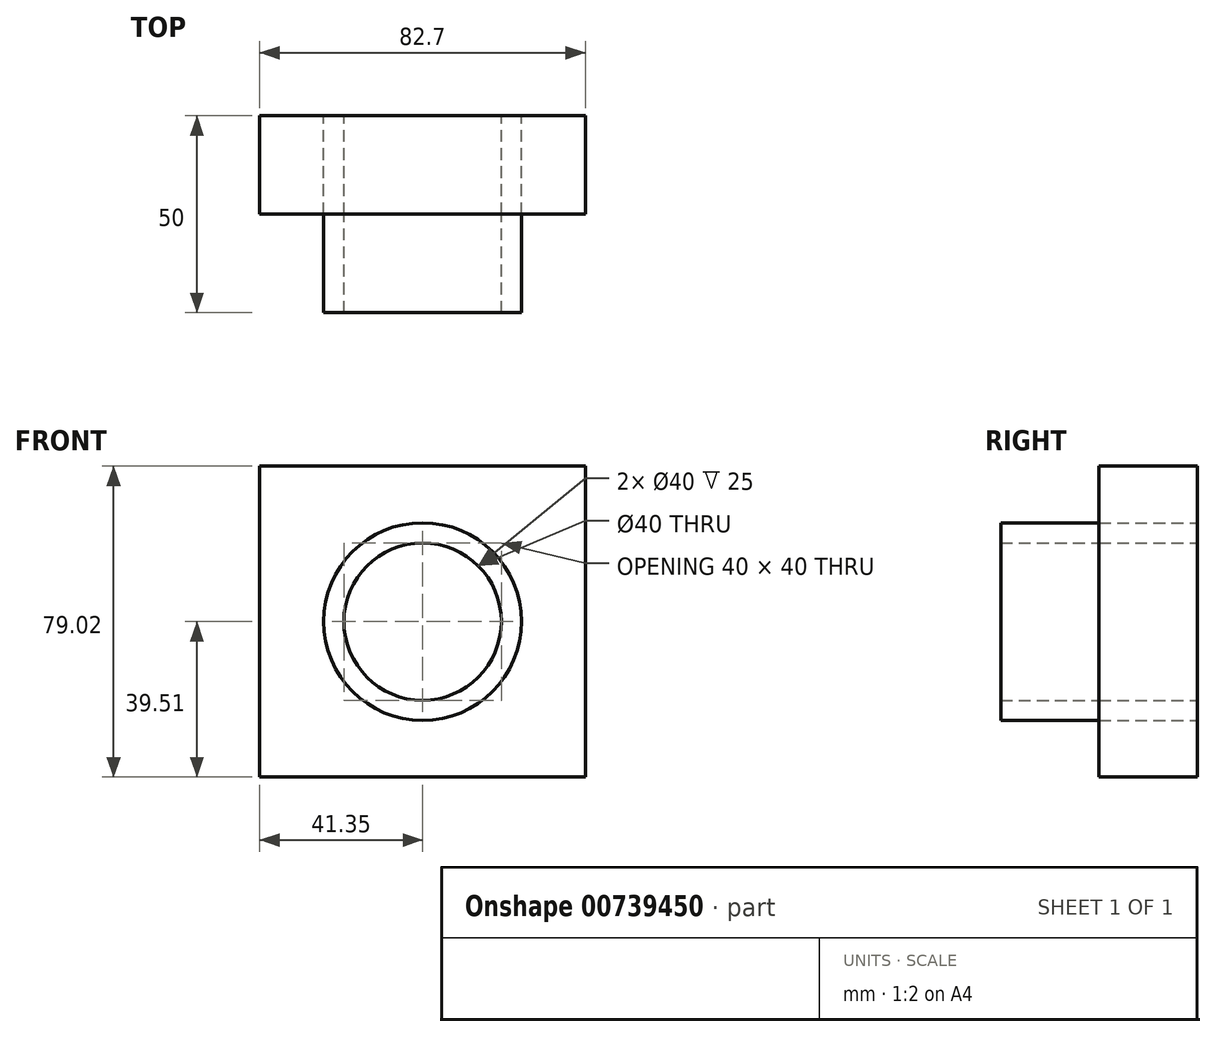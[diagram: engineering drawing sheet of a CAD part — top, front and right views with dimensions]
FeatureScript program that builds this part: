
annotation { "Feature Type Name" : "Feature", "Feature Type Description" : "" }
export const myFeature = defineFeature(function(context is Context, id is Id, definition is map)
    precondition{}
    {
        {
            var Q0;
            Q0=qCreatedBy(makeId("Front.planeOp"),FACE);
            var sketch = newSketch(context, id + "F0", { "sketchPlane" : qUnion([Q0])});
            skLineSegment(sketch, "E0.bottom", {"start": v(41.35, 39.51) * mm, "end": v(-41.35, 39.51) * mm});
            skLineSegment(sketch, "E0.top", {"start": v(41.35, -39.51) * mm, "end": v(-41.35, -39.51) * mm});
            skLineSegment(sketch, "E0.left", {"start": v(41.35, 39.51) * mm, "end": v(41.35, -39.51) * mm});
            skLineSegment(sketch, "E0.right", {"start": v(-41.35, 39.51) * mm, "end": v(-41.35, -39.51) * mm});
            skPoint(sketch, "E0.middle", {"position": v(0, 0) * mm});
            skSolve(sketch);
        }
        {
            var Q0;
            Q0=qCreatedBy(makeId("Front.planeOp"),FACE);
            var sketch = newSketch(context, id + "F1", { "sketchPlane" : qUnion([Q0])});
            skCircle(sketch, "E1", {"center": v(0, 0) * mm, "radius": 25.11 * mm});
            skSolve(sketch);
        }
        {
            var Q0;
            Q0=makeQuery(id+"F0.imprint","IMPRINT",FACE,{"disambiguationData":[TD([[makeQuery(id+"F0.imprint","IMPRINT",EDGE,{"derivedFrom":sQuery(id+"F0.wireOp",EDGE,"E0.bottom")}),1.0]])]});
            var Q1;
            Q1=makeQuery(id+"F1.imprint","IMPRINT",FACE,{"disambiguationData":[TD([[makeQuery(id+"F1.imprint","IMPRINT",EDGE,{"derivedFrom":sQuery(id+"F1.wireOp",EDGE,"E1")}),1.0]])]});
            extrude(context, id + "F2", {"entities" : qUnion([Q0, Q1]), "depth" : 25 * mm, "offsetDistance" : 25 * mm});
        }
        {
            var Q0;
            Q0=makeQuery(id+"F2.opExtrude","CAP_FACE",FACE,{"disambiguationData":[OSD([sQuery(id+"F1.wireOp",EDGE,"E1")])],"isStart":false});
            extrude(context, id + "F3", {"entities" : qUnion([Q0]), "depth" : 25 * mm, "offsetDistance" : 25 * mm});
        }
        {
            var Q0;
            Q0=qCreatedBy(makeId("Front.planeOp"),FACE);
            var sketch = newSketch(context, id + "F4", { "sketchPlane" : qUnion([Q0])});
            skPoint(sketch, "E2", {"position": v(0, 0) * mm});
            skSolve(sketch);
        }
        {
            var Q0;
            Q0=sQuery(id+"F4.wireOp",VERTEX,"E2");
            var Q1;
            Q1=makeQuery(id+"F2.opExtrude","SWEPT_BODY",BODY,{"disambiguationData":[OSD([sQuery(id+"F0.wireOp",EDGE,"E0.bottom"),sQuery(id+"F0.wireOp",EDGE,"E0.top"),sQuery(id+"F0.wireOp",EDGE,"E0.left"),sQuery(id+"F0.wireOp",EDGE,"E0.right")])]});
            var Q2;
            Q2=makeQuery(id+"F2.opExtrude","SWEPT_BODY",BODY,{"disambiguationData":[OSD([sQuery(id+"F1.wireOp",EDGE,"E1")])]});
            var Q3;
            Q3=makeQuery(id+"F3.opExtrude","SWEPT_BODY",BODY,{"disambiguationData":[OSD([sQuery(id+"F1.wireOp",EDGE,"E1")])]});
            hole(context, id + "F5", {"style" : HoleStyle.SIMPLE, "endStyle" : HoleEndStyle.THROUGH, "oppositeDirection" : true, "holeDiameter" : 40 * mm, "majorDiameter" : 5 * mm, "isTappedThrough" : true, "tappedDepth" : 12 * mm, "tapClearance" : 3, "locations" : qUnion([Q0]), "scope" : qUnion([Q1, Q2, Q3])});
        }
    });
